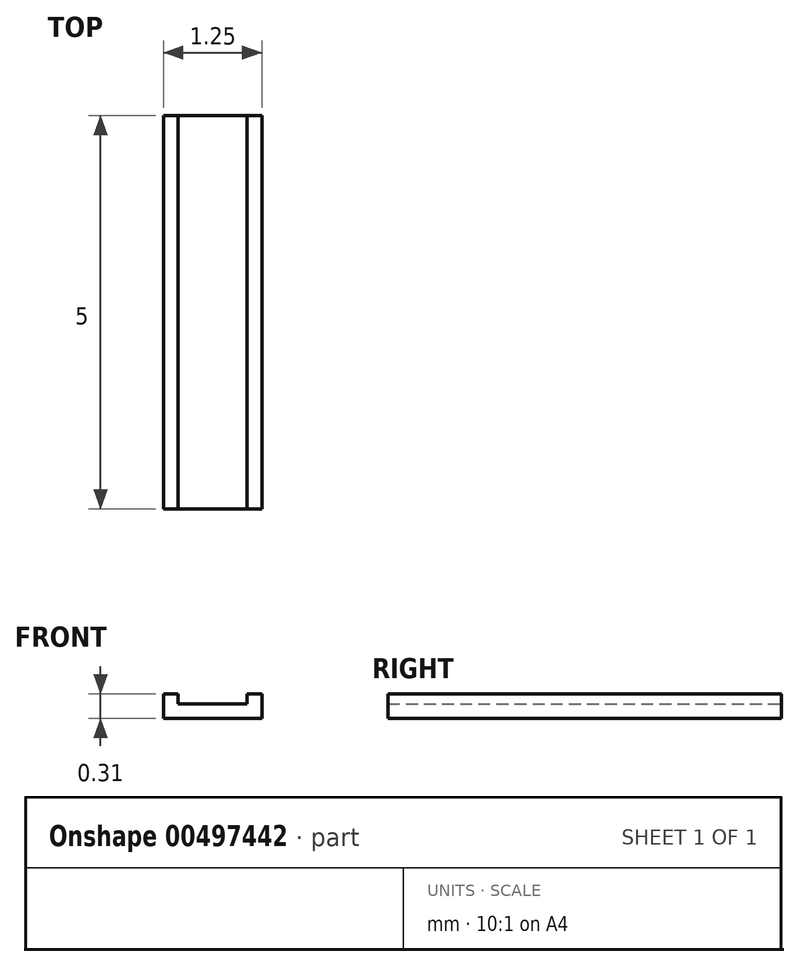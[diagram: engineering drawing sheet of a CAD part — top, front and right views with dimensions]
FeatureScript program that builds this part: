
annotation { "Feature Type Name" : "Feature", "Feature Type Description" : "" }
export const myFeature = defineFeature(function(context is Context, id is Id, definition is map)
    precondition{}
    {
        {
            var Q0;
            Q0=qCreatedBy(makeId("Front.planeOp"),FACE);
            var sketch = newSketch(context, id + "F0", { "sketchPlane" : qUnion([Q0])});
            skLineSegment(sketch, "E0", {"start": v(0, 0) * mm, "end": v(1.25, 0) * mm});
            skLineSegment(sketch, "E1", {"start": v(1.25, 0) * mm, "end": v(1.25, 0.31) * mm});
            skLineSegment(sketch, "E2", {"start": v(0.62, 0) * mm, "end": v(0.62, 0.19) * mm});
            skLineSegment(sketch, "E3", {"start": v(0.62, 0.19) * mm, "end": v(1.06, 0.19) * mm});
            skLineSegment(sketch, "E4", {"start": v(0.62, 0.19) * mm, "end": v(0.19, 0.19) * mm});
            skLineSegment(sketch, "E5", {"start": v(0, 0) * mm, "end": v(0, 0.31) * mm});
            skLineSegment(sketch, "E6", {"start": v(1.06, 0.19) * mm, "end": v(1.06, 0.31) * mm});
            skLineSegment(sketch, "E7", {"start": v(1.25, 0.31) * mm, "end": v(1.06, 0.31) * mm});
            skLineSegment(sketch, "E8", {"start": v(0.19, 0.19) * mm, "end": v(0.19, 0.31) * mm});
            skLineSegment(sketch, "E9", {"start": v(0, 0.31) * mm, "end": v(0.19, 0.31) * mm});
            skSolve(sketch);
        }
        {
            var Q0;
            Q0 = qSketchRegion(id + "F0", true);
            extrude(context, id + "F1", {"entities" : qUnion([Q0]), "depth" : 5 * mm});
        }
    });
